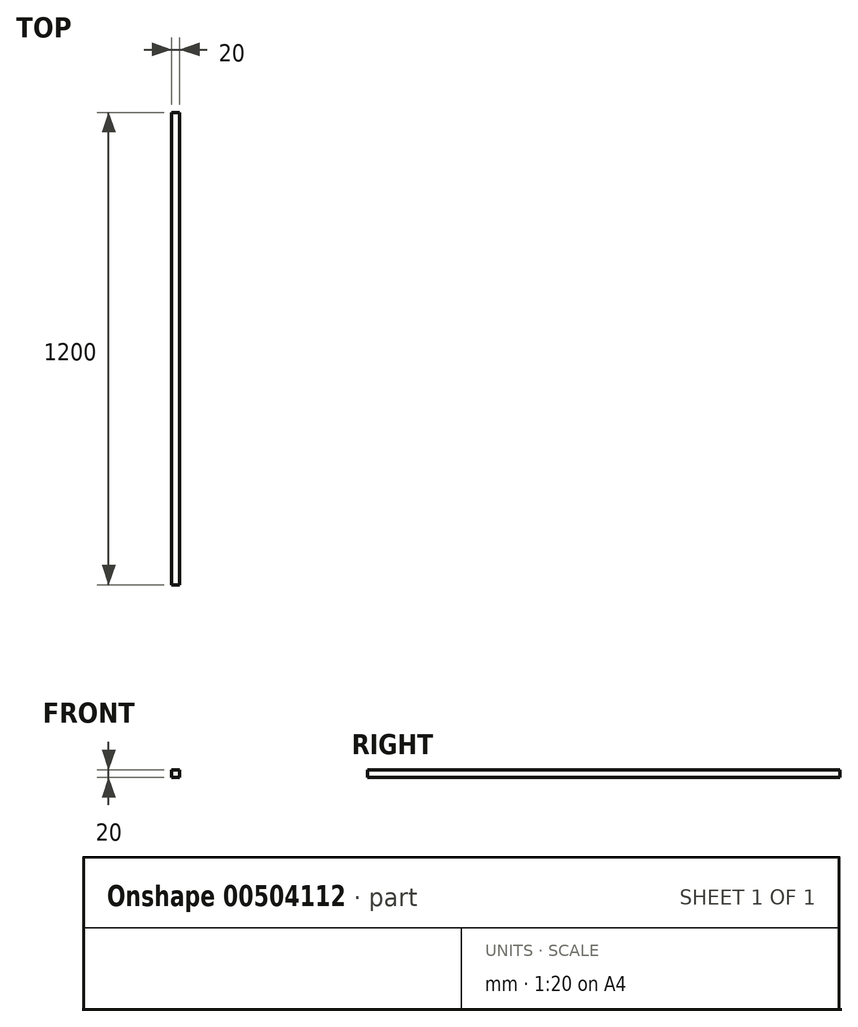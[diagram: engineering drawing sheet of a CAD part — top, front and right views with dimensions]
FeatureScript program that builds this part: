
annotation { "Feature Type Name" : "Feature", "Feature Type Description" : "" }
export const myFeature = defineFeature(function(context is Context, id is Id, definition is map)
    precondition{}
    {
        {
            var Q0;
            Q0=qCreatedBy(makeId("Right.planeOp"),FACE);
            var sketch = newSketch(context, id + "F0", { "sketchPlane" : qUnion([Q0])});
            skLineSegment(sketch, "E0", {"start": v(0, 0) * mm, "end": v(-1200, 0) * mm});
            skSolve(sketch);
        }
        {
            var Q0;
            Q0=qCreatedBy(makeId("Front.planeOp"),FACE);
            var sketch = newSketch(context, id + "F1", { "sketchPlane" : qUnion([Q0])});
            skLineSegment(sketch, "E1.bottom", {"start": v(0, 0) * mm, "end": v(20, 0) * mm});
            skLineSegment(sketch, "E1.top", {"start": v(0, 20) * mm, "end": v(20, 20) * mm});
            skLineSegment(sketch, "E1.left", {"start": v(0, 0) * mm, "end": v(0, 20) * mm});
            skLineSegment(sketch, "E1.right", {"start": v(20, 0) * mm, "end": v(20, 20) * mm});
            skSolve(sketch);
        }
        {
            var Q0;
            Q0=makeQuery(id+"F1.imprint","IMPRINT",FACE,{"disambiguationData":[TD([[makeQuery(id+"F1.imprint","IMPRINT",EDGE,{"derivedFrom":sQuery(id+"F1.wireOp",EDGE,"E1.bottom")}),1.0]])]});
            var Q1;
            Q1=sQuery(id+"F0.wireOp",EDGE,"E0");
            sweep(context, id + "F2", {"profiles" : qUnion([Q0]), "path" : qUnion([Q1])});
        }
    });
